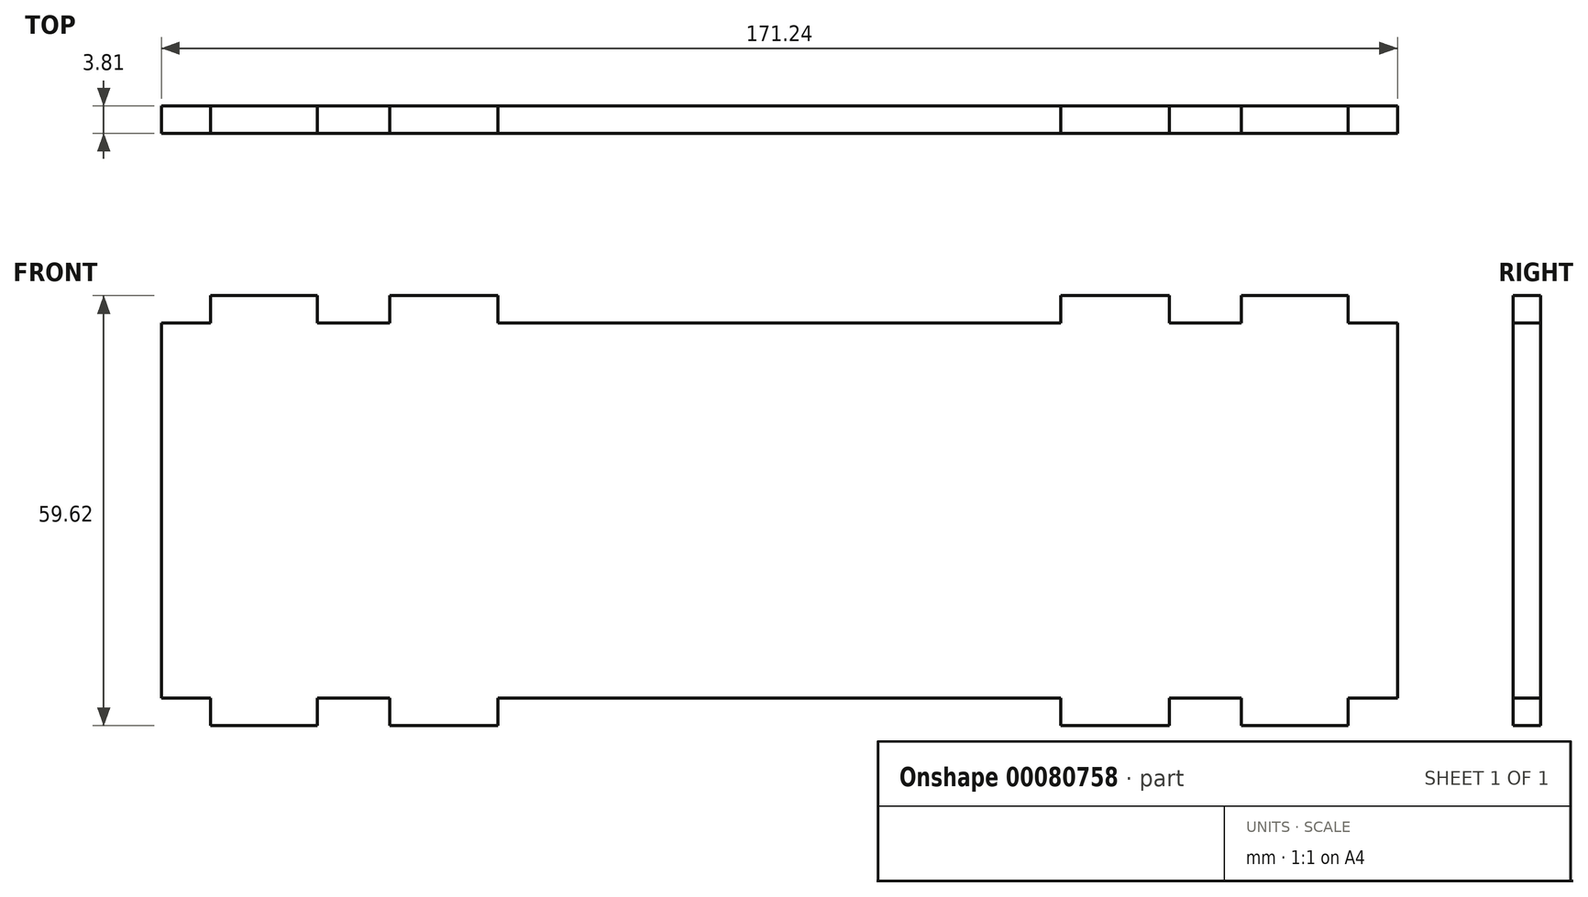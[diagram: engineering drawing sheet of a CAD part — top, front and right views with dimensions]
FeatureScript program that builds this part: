
annotation { "Feature Type Name" : "Feature", "Feature Type Description" : "" }
export const myFeature = defineFeature(function(context is Context, id is Id, definition is map)
    precondition{}
    {
        {
            var Q0;
            Q0=qCreatedBy(makeId("Front.planeOp"),FACE);
            var sketch = newSketch(context, id + "F0", { "sketchPlane" : qUnion([Q0])});
            skLineSegment(sketch, "E0.bottom", {"start": v(85.62, 26) * mm, "end": v(-85.62, 26) * mm});
            skLineSegment(sketch, "E0.top", {"start": v(85.62, -26) * mm, "end": v(-85.62, -26) * mm});
            skLineSegment(sketch, "E0.left", {"start": v(85.62, 26) * mm, "end": v(85.62, -26) * mm});
            skLineSegment(sketch, "E0.right", {"start": v(-85.62, 26) * mm, "end": v(-85.62, -26) * mm});
            skPoint(sketch, "E0.middle", {"position": v(0, 0) * mm});
            skLineSegment(sketch, "E1", {"start": v(0, 26) * mm, "end": v(0, -26) * mm});
            skLineSegment(sketch, "E2", {"start": v(-85.62, 0) * mm, "end": v(85.62, 0) * mm});
            skLineSegment(sketch, "E3.MirrorCS", {"start": v(78.8, 29.8) * mm, "end": v(64, 29.8) * mm});
            skLineSegment(sketch, "E4", {"start": v(64, 29.8) * mm, "end": v(64, 26) * mm});
            skLineSegment(sketch, "E5", {"start": v(78.8, 29.8) * mm, "end": v(78.8, 26) * mm});
            skLineSegment(sketch, "E6.MirrorCS", {"start": v(78.8, -29.8) * mm, "end": v(64, -29.8) * mm});
            skLineSegment(sketch, "E7.MirrorCS", {"start": v(64, -29.8) * mm, "end": v(64, -26) * mm});
            skLineSegment(sketch, "E8.MirrorCS", {"start": v(78.8, -29.8) * mm, "end": v(78.8, -26) * mm});
            skLineSegment(sketch, "E9.MirrorCS", {"start": v(-78.8, 29.8) * mm, "end": v(-64, 29.8) * mm});
            skLineSegment(sketch, "E10.MirrorCS", {"start": v(-64, 29.8) * mm, "end": v(-64, 26) * mm});
            skLineSegment(sketch, "E11.MirrorCS", {"start": v(-78.8, 29.8) * mm, "end": v(-78.8, 26) * mm});
            skLineSegment(sketch, "E12.MirrorCS", {"start": v(-64, -29.8) * mm, "end": v(-64, -26) * mm});
            skLineSegment(sketch, "E13.MirrorCS", {"start": v(-78.8, -29.8) * mm, "end": v(-64, -29.8) * mm});
            skLineSegment(sketch, "E14.MirrorCS", {"start": v(-78.8, -29.8) * mm, "end": v(-78.8, -26) * mm});
            skLineSegment(sketch, "E15", {"start": v(-54, 26) * mm, "end": v(-54, 29.8) * mm});
            skLineSegment(sketch, "E16", {"start": v(-54, 29.8) * mm, "end": v(-39, 29.8) * mm});
            skLineSegment(sketch, "E17", {"start": v(-39, 29.8) * mm, "end": v(-39, 26) * mm});
            skLineSegment(sketch, "E18.MirrorCS", {"start": v(-54, -29.8) * mm, "end": v(-39, -29.8) * mm});
            skLineSegment(sketch, "E19.MirrorCS", {"start": v(-54, -26) * mm, "end": v(-54, -29.8) * mm});
            skLineSegment(sketch, "E20.MirrorCS", {"start": v(-39, -29.8) * mm, "end": v(-39, -26) * mm});
            skLineSegment(sketch, "E21.MirrorCS", {"start": v(54, 29.81) * mm, "end": v(39, 29.8) * mm});
            skLineSegment(sketch, "E22.MirrorCS", {"start": v(39, 29.8) * mm, "end": v(39, 26) * mm});
            skLineSegment(sketch, "E23.MirrorCS", {"start": v(54, 26) * mm, "end": v(54, 29.81) * mm});
            skLineSegment(sketch, "E24.MirrorCS", {"start": v(54, -29.8) * mm, "end": v(39, -29.8) * mm});
            skLineSegment(sketch, "E25.MirrorCS", {"start": v(54, -26) * mm, "end": v(54, -29.8) * mm});
            skLineSegment(sketch, "E26.MirrorCS", {"start": v(39, -29.8) * mm, "end": v(39, -26) * mm});
            skSolve(sketch);
        }
        {
            var Q0;
            Q0=makeQuery(id+"F0.imprint","IMPRINT",FACE,{"disambiguationData":[TD([[makeQuery(id+"F0.imprint","IMPRINT",EDGE,{"derivedFrom":sQuery(id+"F0.wireOp",EDGE,"E0.bottom")}),1.0]])]});
            var Q1;
            {var subQ0=sQuery(id+"F0.wireOp",EDGE,"fd9a9881-1114-4a34-881d-6aab33066d9a0.MirrorCS");Q1=makeQuery(id+"F0.imprint","IMPRINT",FACE,{"disambiguationData":[TD([[makeQuery(id+"F0.imprint","IMPRINT",EDGE,{"derivedFrom":subQ0}),-1.0]])]});}
            var Q2;
            Q2=makeQuery(id+"F0.imprint","IMPRINT",FACE,{"disambiguationData":[TD([[makeQuery(id+"F0.imprint","IMPRINT",EDGE,{"derivedFrom":sQuery(id+"F0.wireOp",EDGE,"e9cbb39e-25d4-43ef-8b23-404016609ed90.MirrorCS")}),1.0]])]});
            var Q3;
            {var subQ0=sQuery(id+"F0.wireOp",EDGE,"E0.top");var subQ9=sQuery(id+"F0.wireOp",EDGE,"E1");var subQ10=makeQuery(id+"F0.imprint","INTERSECT",VERTEX,{"derivedFrom":[subQ0,subQ9]});Q3=makeQuery(id+"F0.imprint","IMPRINT",FACE,{"disambiguationData":[TD([[makeQuery(id+"F0.imprint","IMPRINT",EDGE,{"disambiguationData":[TD([[subQ10,-1.0]])],"derivedFrom":subQ0}),-1.0]])]});}
            var Q4;
            {var subQ0=sQuery(id+"F0.wireOp",EDGE,"E0.top");var subQ5=sQuery(id+"F0.wireOp",EDGE,"E0.left");var subQ6=makeQuery(id+"F0.imprint","INTERSECT",VERTEX,{"derivedFrom":[subQ0,subQ5]});Q4=makeQuery(id+"F0.imprint","IMPRINT",FACE,{"disambiguationData":[TD([[makeQuery(id+"F0.imprint","IMPRINT",EDGE,{"disambiguationData":[TD([[subQ6,-1.0]])],"derivedFrom":subQ0}),-1.0]])]});}
            var Q5;
            {var subQ0=sQuery(id+"F0.wireOp",EDGE,"401eab21-d0eb-4b6a-999c-0202608270cc0.MirrorCS");Q5=makeQuery(id+"F0.imprint","IMPRINT",FACE,{"disambiguationData":[TD([[makeQuery(id+"F0.imprint","IMPRINT",EDGE,{"derivedFrom":subQ0}),-1.0]])]});}
            var Q6;
            Q6=makeQuery(id+"F0.imprint","IMPRINT",FACE,{"disambiguationData":[TD([[makeQuery(id+"F0.imprint","IMPRINT",EDGE,{"derivedFrom":sQuery(id+"F0.wireOp",EDGE,"30391e0d-861b-499c-bc64-7791a20e464f0.MirrorCS")}),-1.0]])]});
            var Q7;
            {var subQ0=sQuery(id+"F0.wireOp",EDGE,"6473a4aa-d753-4074-8c14-d968af5e0e340.MirrorCS");Q7=makeQuery(id+"F0.imprint","IMPRINT",FACE,{"disambiguationData":[TD([[makeQuery(id+"F0.imprint","IMPRINT",EDGE,{"derivedFrom":subQ0}),-1.0]])]});}
            var Q8;
            Q8=makeQuery(id+"F0.imprint","IMPRINT",FACE,{"disambiguationData":[TD([[makeQuery(id+"F0.imprint","IMPRINT",EDGE,{"derivedFrom":sQuery(id+"F0.wireOp",EDGE,"fecd9772-fa22-4386-91d1-5c1f6a4e36900.MirrorCS")}),1.0]])]});
            var Q9;
            Q9=makeQuery(id+"F0.imprint","IMPRINT",FACE,{"disambiguationData":[TD([[makeQuery(id+"F0.imprint","IMPRINT",EDGE,{"derivedFrom":sQuery(id+"F0.wireOp",EDGE,"5e35dc9c-8b32-406b-8670-51bc3dacd16a0.MirrorCS")}),-1.0]])]});
            var Q10;
            Q10=makeQuery(id+"F0.imprint","IMPRINT",FACE,{"disambiguationData":[TD([[makeQuery(id+"F0.imprint","IMPRINT",EDGE,{"derivedFrom":sQuery(id+"F0.wireOp",EDGE,"d01f1c85-b5f6-4cd6-8d75-d1ca25df48720.MirrorCS")}),-1.0]])]});
            var Q11;
            {var subQ0=sQuery(id+"F0.wireOp",EDGE,"64aee7ef-a2d6-4a05-a809-71a0f63b7b4d0.MirrorCS");Q11=makeQuery(id+"F0.imprint","IMPRINT",FACE,{"disambiguationData":[TD([[makeQuery(id+"F0.imprint","IMPRINT",EDGE,{"derivedFrom":subQ0}),-1.0]])]});}
            var Q12;
            Q12=makeQuery(id+"F0.imprint","IMPRINT",FACE,{"disambiguationData":[TD([[makeQuery(id+"F0.imprint","IMPRINT",EDGE,{"derivedFrom":sQuery(id+"F0.wireOp",EDGE,"E3.MirrorCS")}),1.0]])]});
            var Q13;
            Q13=makeQuery(id+"F0.imprint","IMPRINT",FACE,{"disambiguationData":[TD([[makeQuery(id+"F0.imprint","IMPRINT",EDGE,{"derivedFrom":sQuery(id+"F0.wireOp",EDGE,"5e85ca08-a0c1-4344-8977-c1e94523da100.MirrorCS")}),1.0]])]});
            var Q14;
            Q14=makeQuery(id+"F0.imprint","IMPRINT",FACE,{"disambiguationData":[TD([[makeQuery(id+"F0.imprint","IMPRINT",EDGE,{"derivedFrom":sQuery(id+"F0.wireOp",EDGE,"6f26e7cf-d43b-4aba-8b23-2f0c2296f61f0.MirrorCS")}),1.0]])]});
            var Q15;
            {var subQ0=sQuery(id+"F0.wireOp",EDGE,"E12.MirrorCS");Q15=makeQuery(id+"F0.imprint","IMPRINT",FACE,{"disambiguationData":[TD([[makeQuery(id+"F0.imprint","IMPRINT",EDGE,{"derivedFrom":subQ0}),1.0]])]});}
            var Q16;
            Q16=makeQuery(id+"F0.imprint","IMPRINT",FACE,{"disambiguationData":[TD([[makeQuery(id+"F0.imprint","IMPRINT",EDGE,{"derivedFrom":sQuery(id+"F0.wireOp",EDGE,"71418182-0ad3-425f-ac6c-b0ad9801f65d0.MirrorCS")}),1.0]])]});
            var Q17;
            Q17=makeQuery(id+"F0.imprint","IMPRINT",FACE,{"disambiguationData":[TD([[makeQuery(id+"F0.imprint","IMPRINT",EDGE,{"derivedFrom":sQuery(id+"F0.wireOp",EDGE,"E9.MirrorCS")}),-1.0]])]});
            var Q18;
            Q18=makeQuery(id+"F0.imprint","IMPRINT",FACE,{"disambiguationData":[TD([[makeQuery(id+"F0.imprint","IMPRINT",EDGE,{"derivedFrom":sQuery(id+"F0.wireOp",EDGE,"0c83b9c4-936b-4906-90ef-ea555f0fafea0.MirrorCS")}),-1.0]])]});
            var Q19;
            Q19=makeQuery(id+"F0.imprint","IMPRINT",FACE,{"disambiguationData":[TD([[makeQuery(id+"F0.imprint","IMPRINT",EDGE,{"derivedFrom":sQuery(id+"F0.wireOp",EDGE,"E6.MirrorCS")}),-1.0]])]});
            var Q20;
            {var subQ0=sQuery(id+"F0.wireOp",EDGE,"E15");Q20=makeQuery(id+"F0.imprint","IMPRINT",FACE,{"disambiguationData":[TD([[makeQuery(id+"F0.imprint","IMPRINT",EDGE,{"derivedFrom":subQ0}),-1.0]])]});}
            var Q21;
            Q21=makeQuery(id+"F0.imprint","IMPRINT",FACE,{"disambiguationData":[TD([[makeQuery(id+"F0.imprint","IMPRINT",EDGE,{"derivedFrom":sQuery(id+"F0.wireOp",EDGE,"E18.MirrorCS")}),1.0]])]});
            var Q22;
            Q22=makeQuery(id+"F0.imprint","IMPRINT",FACE,{"disambiguationData":[TD([[makeQuery(id+"F0.imprint","IMPRINT",EDGE,{"derivedFrom":sQuery(id+"F0.wireOp",EDGE,"E24.MirrorCS")}),-1.0]])]});
            var Q23;
            Q23=makeQuery(id+"F0.imprint","IMPRINT",FACE,{"disambiguationData":[TD([[makeQuery(id+"F0.imprint","IMPRINT",EDGE,{"derivedFrom":sQuery(id+"F0.wireOp",EDGE,"E21.MirrorCS")}),1.0]])]});
            extrude(context, id + "F1", {"entities" : qUnion([Q0, Q1, Q2, Q3, Q4, Q5, Q6, Q7, Q8, Q9, Q10, Q11, Q12, Q13, Q14, Q15, Q16, Q17, Q18, Q19, Q20, Q21, Q22, Q23]), "depth" : 3.8 * mm});
        }
    });
